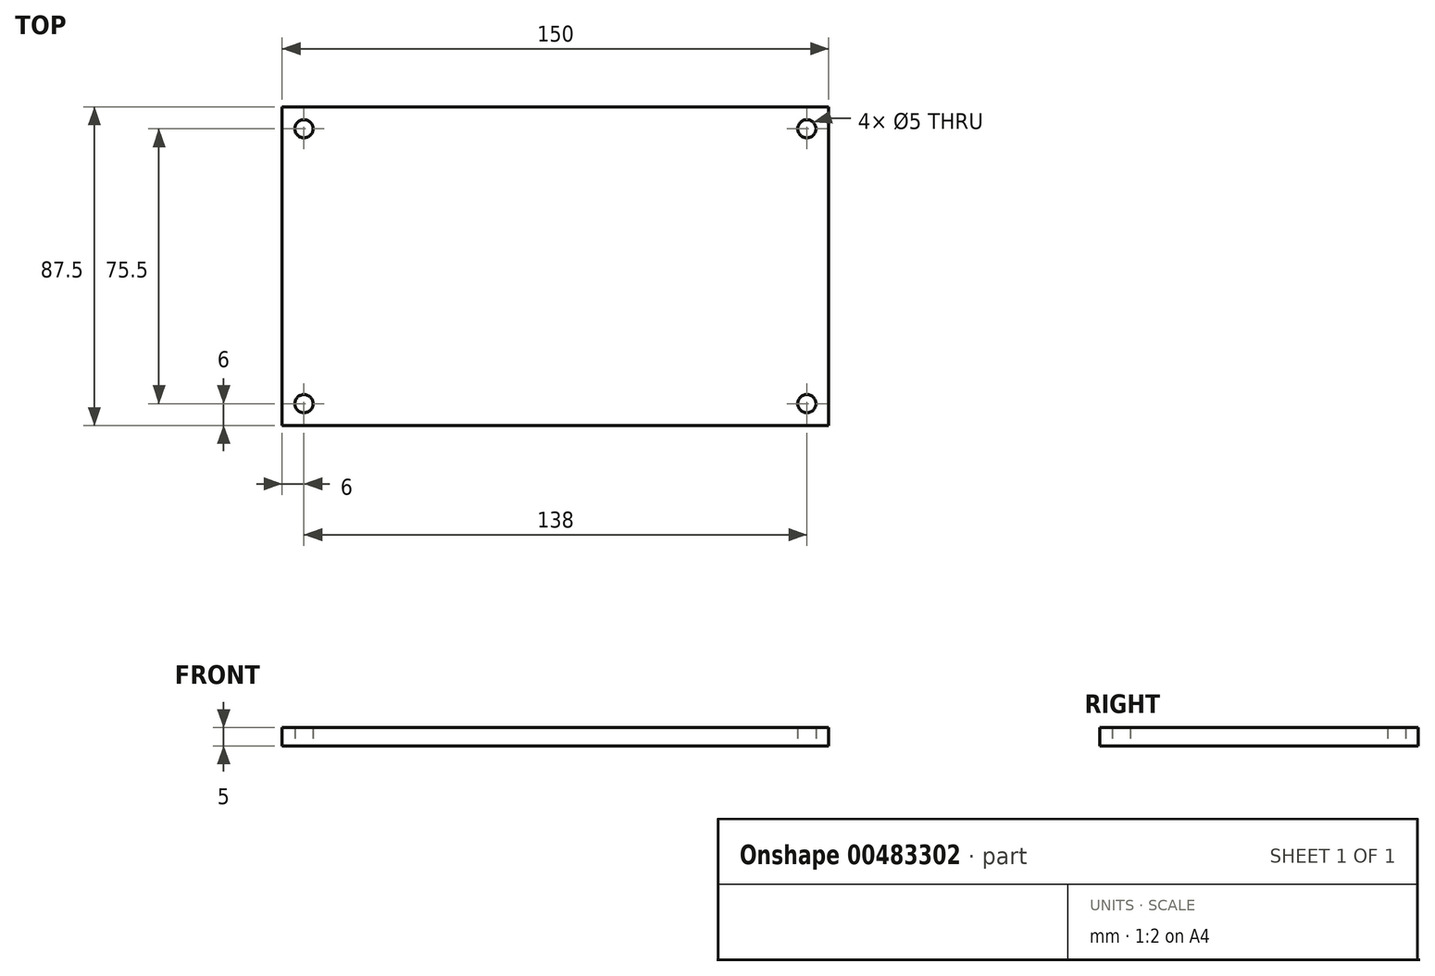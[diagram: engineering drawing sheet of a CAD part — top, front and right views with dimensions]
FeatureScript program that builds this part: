
annotation { "Feature Type Name" : "Feature", "Feature Type Description" : "" }
export const myFeature = defineFeature(function(context is Context, id is Id, definition is map)
    precondition{}
    {
        {
            var Q0;
            Q0=qCreatedBy(makeId("Top.planeOp"),FACE);
            var sketch = newSketch(context, id + "F0", { "sketchPlane" : qUnion([Q0])});
            skLineSegment(sketch, "E0.bottom", {"start": v(69, 37.75) * mm, "end": v(-69, 37.75) * mm});
            skLineSegment(sketch, "E0.top", {"start": v(69, -37.75) * mm, "end": v(-69, -37.75) * mm});
            skLineSegment(sketch, "E0.left", {"start": v(69, 37.75) * mm, "end": v(69, -37.75) * mm});
            skLineSegment(sketch, "E0.right", {"start": v(-69, 37.75) * mm, "end": v(-69, -37.75) * mm});
            skPoint(sketch, "E0.middle", {"position": v(0, 0) * mm});
            skCircle(sketch, "E1", {"center": v(-69, 37.75) * mm, "radius": 2.5 * mm});
            skCircle(sketch, "E2", {"center": v(69, 37.75) * mm, "radius": 2.5 * mm});
            skCircle(sketch, "E3", {"center": v(-69, -37.75) * mm, "radius": 2.5 * mm});
            skCircle(sketch, "E4", {"center": v(69, -37.75) * mm, "radius": 2.5 * mm});
            skLineSegment(sketch, "E5.0", {"start": v(75, 43.75) * mm, "end": v(-75, 43.75) * mm});
            skLineSegment(sketch, "E5.1", {"start": v(75, 43.75) * mm, "end": v(75, -43.75) * mm});
            skLineSegment(sketch, "E5.2", {"start": v(75, -43.75) * mm, "end": v(-75, -43.75) * mm});
            skLineSegment(sketch, "E5.3", {"start": v(-75, 43.75) * mm, "end": v(-75, -43.75) * mm});
            skSolve(sketch);
        }
        {
            var Q0;
            {var subQ5=sQuery(id+"F0.wireOp",EDGE,"E2");var subQ13=sQuery(id+"F0.wireOp",EDGE,"E0.bottom");var subQ14=makeQuery(id+"F0.imprint","INTERSECT",VERTEX,{"derivedFrom":[subQ13,subQ5]});Q0=makeQuery(id+"F0.imprint","IMPRINT",FACE,{"disambiguationData":[TD([[makeQuery(id+"F0.imprint","IMPRINT",EDGE,{"disambiguationData":[TD([[subQ14,-1.0]])],"derivedFrom":subQ13}),1.0]])]});}
            var Q1;
            Q1=makeQuery(id+"F0.imprint","IMPRINT",FACE,{"disambiguationData":[TD([[makeQuery(id+"F0.imprint","IMPRINT",EDGE,{"derivedFrom":sQuery(id+"F0.wireOp",EDGE,"E5.0")}),1.0]])]});
            extrude(context, id + "F1", {"entities" : qUnion([Q0, Q1]), "depth" : 5 * mm});
        }
    });
